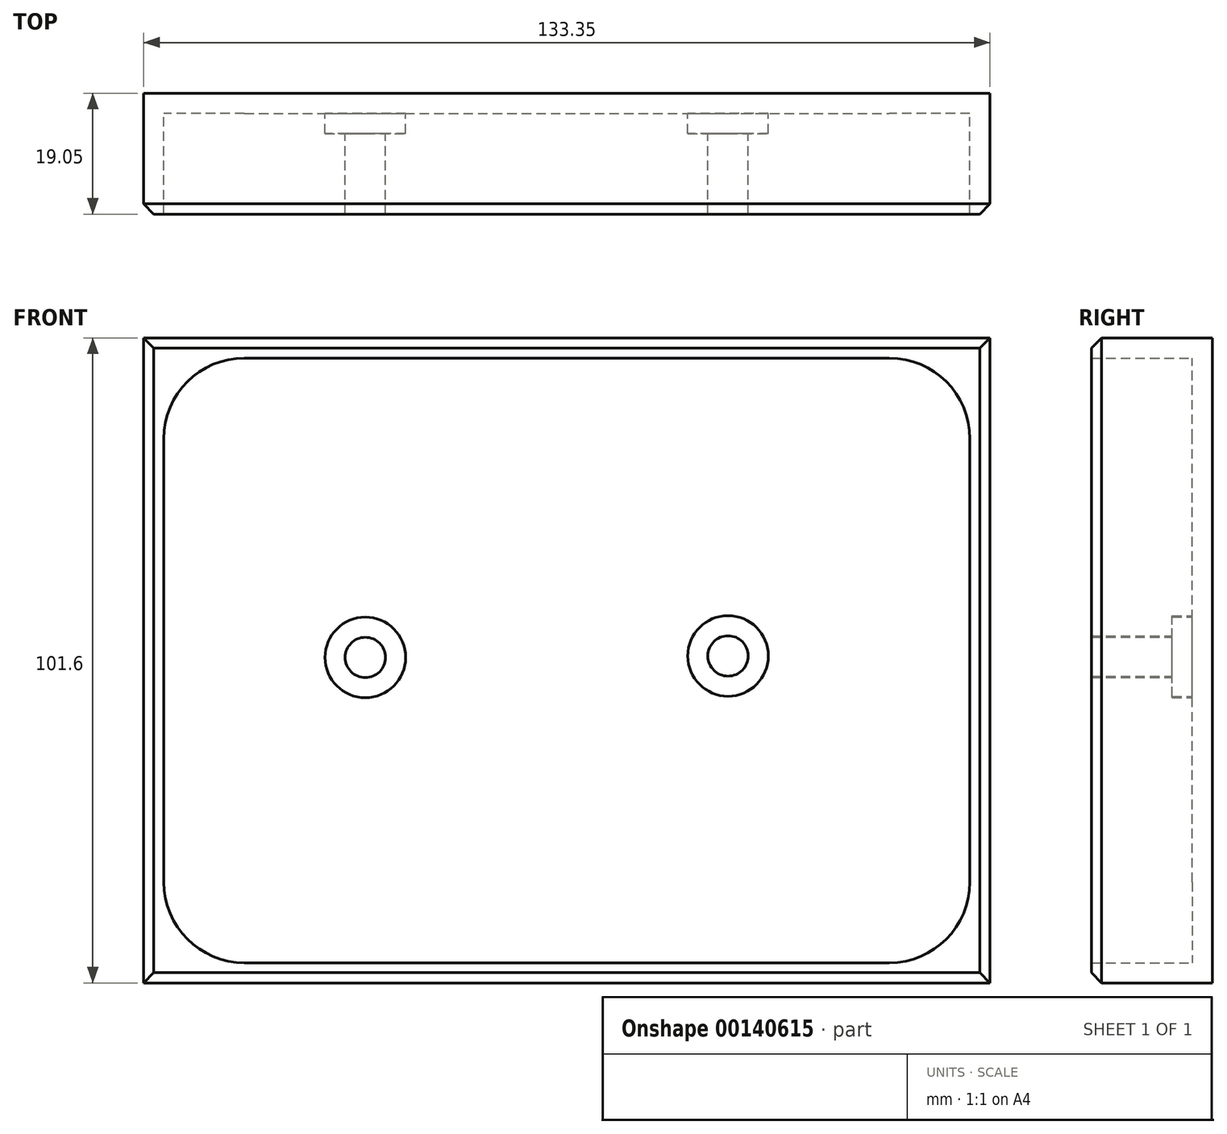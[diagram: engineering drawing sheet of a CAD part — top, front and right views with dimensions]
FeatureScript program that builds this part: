
annotation { "Feature Type Name" : "Feature", "Feature Type Description" : "" }
export const myFeature = defineFeature(function(context is Context, id is Id, definition is map)
    precondition{}
    {
        {
            var Q0;
            Q0=qCreatedBy(makeId("Front.planeOp"),FACE);
            var sketch = newSketch(context, id + "F0", { "sketchPlane" : qUnion([Q0])});
            skLineSegment(sketch, "E0.bottom", {"start": v(0, 0) * mm, "end": v(133.35, 0) * mm});
            skLineSegment(sketch, "E0.top", {"start": v(0, 101.6) * mm, "end": v(133.35, 101.6) * mm});
            skLineSegment(sketch, "E0.left", {"start": v(0, 0) * mm, "end": v(0, 101.6) * mm});
            skLineSegment(sketch, "E0.right", {"start": v(133.35, 0) * mm, "end": v(133.35, 101.6) * mm});
            skSolve(sketch);
        }
        {
            var Q0;
            Q0 = qSketchRegion(id + "F0", true);
            extrude(context, id + "F1", {"entities" : qUnion([Q0]), "depth" : 19.05 * mm});
        }
        {
            var Q0;
            Q0=makeQuery(id+"F1.opExtrude","CAP_FACE",FACE,{"disambiguationData":[OSD([sQuery(id+"F0.wireOp",EDGE,"E0.bottom"),sQuery(id+"F0.wireOp",EDGE,"E0.top"),sQuery(id+"F0.wireOp",EDGE,"E0.left"),sQuery(id+"F0.wireOp",EDGE,"E0.right")])],"isStart":false});
            shell(context, id + "F2", {"entities" : qUnion([Q0]), "thickness" : 3.17 * mm});
        }
        {
            var Q0;
            Q0=makeQuery(id+"F2.opShell","OFFSET_FACE",FACE,{"disambiguationData":[OSD([sQuery(id+"F0.wireOp",EDGE,"E0.bottom"),sQuery(id+"F0.wireOp",EDGE,"E0.top"),sQuery(id+"F0.wireOp",EDGE,"E0.left"),sQuery(id+"F0.wireOp",EDGE,"E0.right")])]});
            var sketch = newSketch(context, id + "F3", { "sketchPlane" : qUnion([Q0])});
            skCircle(sketch, "E1", {"center": v(34.92, 51.26) * mm, "radius": 6.35 * mm});
            skCircle(sketch, "E2", {"center": v(92.07, 51.5) * mm, "radius": 6.35 * mm});
            skLineSegment(sketch, "E3", {"start": v(34.92, 51.26) * mm, "end": v(3.17, 51.26) * mm, "construction": true});
            skSolve(sketch);
        }
        {
            var Q0;
            Q0 = qSketchRegion(id + "F3", true);
            extrude(context, id + "F4", {"entities" : qUnion([Q0]), "operationType" : NewBodyOperationType.ADD, "depth" : 3.17 * mm});
        }
        {
            var Q0;
            Q0=makeQuery(id+"F4.opExtrude","CAP_FACE",FACE,{"disambiguationData":[OSD([sQuery(id+"F3.wireOp",EDGE,"E1")])],"isStart":false});
            var sketch = newSketch(context, id + "F5", { "sketchPlane" : qUnion([Q0])});
            skCircle(sketch, "E4", {"center": v(34.92, 51.26) * mm, "radius": 3.18 * mm});
            skSolve(sketch);
        }
        {
            var Q0;
            Q0 = qSketchRegion(id + "F5", true);
            extrude(context, id + "F6", {"entities" : qUnion([Q0]), "operationType" : NewBodyOperationType.ADD, "depth" : 12.7 * mm});
        }
        {
            var Q0;
            Q0=makeQuery(id+"F4.opExtrude","CAP_FACE",FACE,{"disambiguationData":[OSD([sQuery(id+"F3.wireOp",EDGE,"E2")])],"isStart":false});
            var sketch = newSketch(context, id + "F7", { "sketchPlane" : qUnion([Q0])});
            skCircle(sketch, "E5", {"center": v(92.07, 51.5) * mm, "radius": 3.18 * mm});
            skSolve(sketch);
        }
        {
            var Q0;
            Q0 = qSketchRegion(id + "F7", true);
            extrude(context, id + "F8", {"entities" : qUnion([Q0]), "operationType" : NewBodyOperationType.ADD, "depth" : 12.7 * mm});
        }
        {
            var Q0;
            Q0=makeQuery(id+"F2.opShell","OFFSET_EDGE",EDGE,{"disambiguationData":[OSD([sQuery(id+"F0.wireOp",EDGE,"E0.bottom"),sQuery(id+"F0.wireOp",EDGE,"E0.left")])]});
            var Q1;
            Q1=makeQuery(id+"F2.opShell","OFFSET_EDGE",EDGE,{"disambiguationData":[OSD([sQuery(id+"F0.wireOp",EDGE,"E0.top"),sQuery(id+"F0.wireOp",EDGE,"E0.left")])]});
            var Q2;
            Q2=makeQuery(id+"F2.opShell","OFFSET_EDGE",EDGE,{"disambiguationData":[OSD([sQuery(id+"F0.wireOp",EDGE,"E0.bottom"),sQuery(id+"F0.wireOp",EDGE,"E0.right")])]});
            var Q3;
            Q3=makeQuery(id+"F2.opShell","OFFSET_EDGE",EDGE,{"disambiguationData":[OSD([sQuery(id+"F0.wireOp",EDGE,"E0.top"),sQuery(id+"F0.wireOp",EDGE,"E0.right")])]});
            fillet(context, id + "F9", {"entities" : qUnion([Q0, Q1, Q2, Q3]), "radius" : 12.7 * mm, "tangentPropagation" : true, "allowEdgeOverflow" : false});
        }
        {
            var Q0;
            Q0=makeQuery(id+"F1.opExtrude","CAP_EDGE",EDGE,{"disambiguationData":[OSD([sQuery(id+"F0.wireOp",EDGE,"E0.right")])],"isStart":false});
            var Q1;
            Q1=makeQuery(id+"F1.opExtrude","CAP_EDGE",EDGE,{"disambiguationData":[OSD([sQuery(id+"F0.wireOp",EDGE,"E0.bottom")])],"isStart":false});
            var Q2;
            Q2=makeQuery(id+"F1.opExtrude","CAP_EDGE",EDGE,{"disambiguationData":[OSD([sQuery(id+"F0.wireOp",EDGE,"E0.left")])],"isStart":false});
            var Q3;
            Q3=makeQuery(id+"F1.opExtrude","CAP_EDGE",EDGE,{"disambiguationData":[OSD([sQuery(id+"F0.wireOp",EDGE,"E0.top")])],"isStart":false});
            chamfer(context, id + "F10", {"entities" : qUnion([Q0, Q1, Q2, Q3]), "width" : 1.6 * mm, "tangentPropagation" : true});
        }
    });
